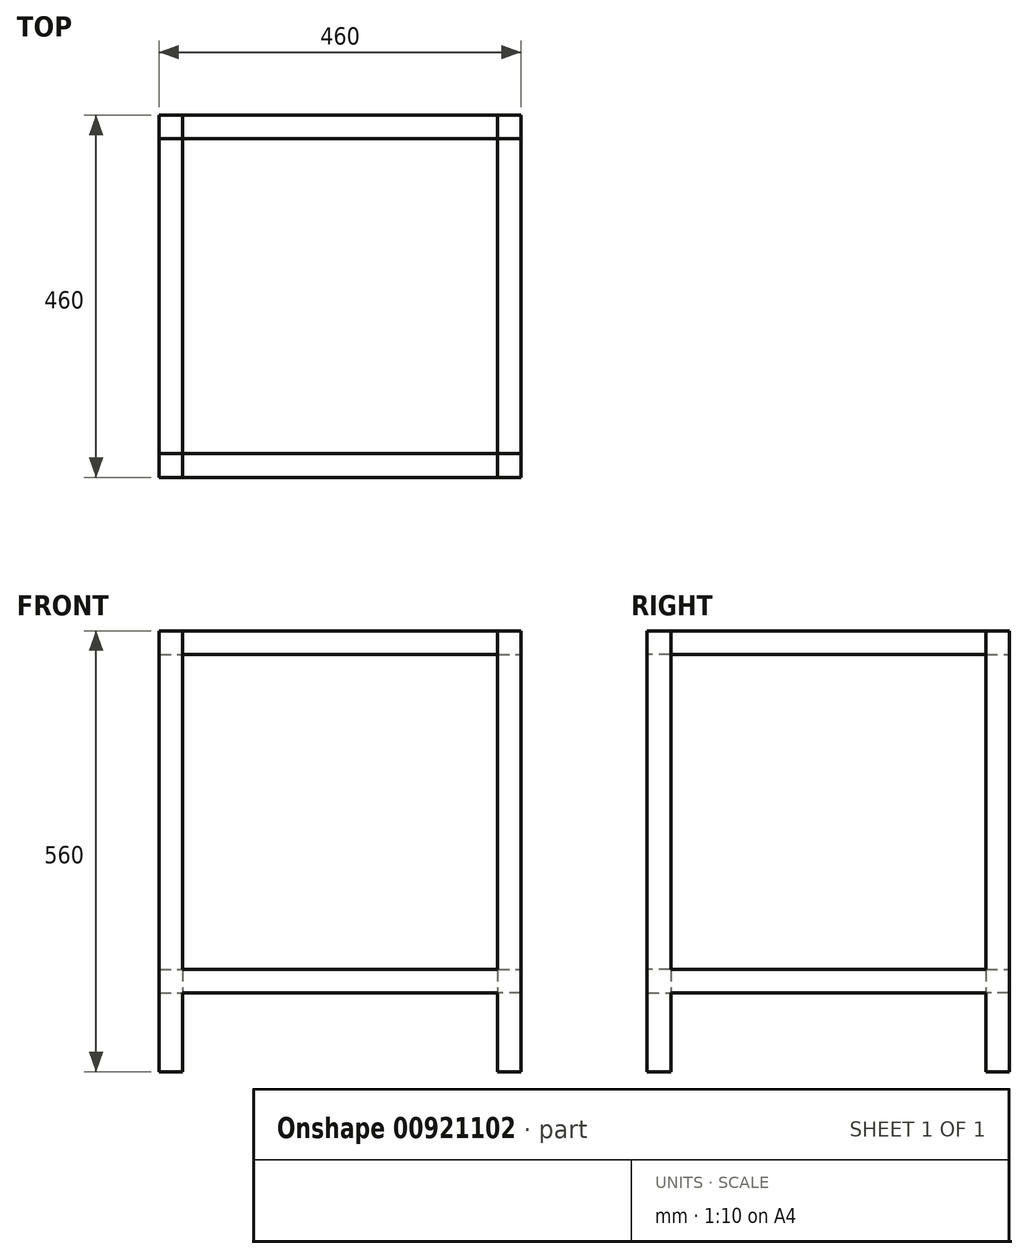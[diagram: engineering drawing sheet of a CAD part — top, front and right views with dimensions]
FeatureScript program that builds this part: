
annotation { "Feature Type Name" : "Feature", "Feature Type Description" : "" }
export const myFeature = defineFeature(function(context is Context, id is Id, definition is map)
    precondition{}
    {
        {
            assignVariable(context, id + "F0", {"variableType" : VariableType.LENGTH, "name" : "cubeInnerLength", "lengthValue" : 400 * mm});
        }
        {
            assignVariable(context, id + "F1", {"variableType" : VariableType.LENGTH, "name" : "aluminumProfileWidth", "lengthValue" : 30 * mm});
        }
        {
            assignVariable(context, id + "F2", {"variableType" : VariableType.LENGTH, "name" : "baseHeight", "lengthValue" : 100 * mm});
        }
        {
            var Q0;
            Q0=qCreatedBy(makeId("Top.planeOp"),FACE);
            var sketch = newSketch(context, id + "F3", { "sketchPlane" : qUnion([Q0])});
            skPoint(sketch, "E0.middle", {"position": v(0, 0) * mm});
            skLineSegment(sketch, "E1.bottom", {"start": v(-230, 230) * mm, "end": v(-200, 230) * mm});
            skLineSegment(sketch, "E1.top", {"start": v(-230, 200) * mm, "end": v(-200, 200) * mm});
            skLineSegment(sketch, "E1.left", {"start": v(-230, 230) * mm, "end": v(-230, 200) * mm});
            skLineSegment(sketch, "E1.right", {"start": v(-200, 230) * mm, "end": v(-200, 200) * mm});
            skLineSegment(sketch, "E2.bottom", {"start": v(230, 230) * mm, "end": v(200, 230) * mm});
            skLineSegment(sketch, "E2.top", {"start": v(230, 200) * mm, "end": v(200, 200) * mm});
            skLineSegment(sketch, "E2.left", {"start": v(230, 230) * mm, "end": v(230, 200) * mm});
            skLineSegment(sketch, "E2.right", {"start": v(200, 230) * mm, "end": v(200, 200) * mm});
            skLineSegment(sketch, "E3.bottom", {"start": v(230, -230) * mm, "end": v(200, -230) * mm});
            skLineSegment(sketch, "E3.top", {"start": v(230, -200) * mm, "end": v(200, -200) * mm});
            skLineSegment(sketch, "E3.left", {"start": v(230, -230) * mm, "end": v(230, -200) * mm});
            skLineSegment(sketch, "E3.right", {"start": v(200, -230) * mm, "end": v(200, -200) * mm});
            skLineSegment(sketch, "E4.bottom", {"start": v(-230, -230) * mm, "end": v(-200, -230) * mm});
            skLineSegment(sketch, "E4.top", {"start": v(-230, -200) * mm, "end": v(-200, -200) * mm});
            skLineSegment(sketch, "E4.left", {"start": v(-230, -230) * mm, "end": v(-230, -200) * mm});
            skLineSegment(sketch, "E4.right", {"start": v(-200, -230) * mm, "end": v(-200, -200) * mm});
            skLineSegment(sketch, "E5.bottom", {"start": v(-200, 200) * mm, "end": v(200, 200) * mm, "construction": true});
            skLineSegment(sketch, "E5.top", {"start": v(-200, -200) * mm, "end": v(200, -200) * mm, "construction": true});
            skLineSegment(sketch, "E5.left", {"start": v(-200, 200) * mm, "end": v(-200, -200) * mm, "construction": true});
            skLineSegment(sketch, "E5.right", {"start": v(200, 200) * mm, "end": v(200, -200) * mm, "construction": true});
            skSolve(sketch);
        }
        {
            var Q0;
            {var subQ4=sQuery(id+"F3.wireOp",EDGE,"E1.top");Q0=makeQuery(id+"F3.imprint","IMPRINT",FACE,{"disambiguationData":[TD([[makeQuery(id+"F3.imprint","IMPRINT",EDGE,{"derivedFrom":subQ4}),1.0]])]});}
            var Q1;
            {var subQ4=sQuery(id+"F3.wireOp",EDGE,"E2.top");Q1=makeQuery(id+"F3.imprint","IMPRINT",FACE,{"disambiguationData":[TD([[makeQuery(id+"F3.imprint","IMPRINT",EDGE,{"derivedFrom":subQ4}),-1.0]])]});}
            var Q2;
            {var subQ4=sQuery(id+"F3.wireOp",EDGE,"E3.top");Q2=makeQuery(id+"F3.imprint","IMPRINT",FACE,{"disambiguationData":[TD([[makeQuery(id+"F3.imprint","IMPRINT",EDGE,{"derivedFrom":subQ4}),1.0]])]});}
            var Q3;
            {var subQ4=sQuery(id+"F3.wireOp",EDGE,"E4.top");Q3=makeQuery(id+"F3.imprint","IMPRINT",FACE,{"disambiguationData":[TD([[makeQuery(id+"F3.imprint","IMPRINT",EDGE,{"derivedFrom":subQ4}),-1.0]])]});}
            extrude(context, id + "F4", {"entities" : qUnion([Q0, Q1, Q2, Q3]), "depth" : getVariable(context, 'cubeInnerLength') + 2 * getVariable(context, 'aluminumProfileWidth'), "offsetDistance" : 25 * mm, "symmetric" : true});
        }
        {
            var Q0;
            Q0=qCreatedBy(makeId("Front.planeOp"),FACE);
            var sketch = newSketch(context, id + "F5", { "sketchPlane" : qUnion([Q0])});
            skLineSegment(sketch, "E6.bottom", {"start": v(-230, 230) * mm, "end": v(-200, 230) * mm});
            skLineSegment(sketch, "E6.top", {"start": v(-230, 200) * mm, "end": v(-200, 200) * mm});
            skLineSegment(sketch, "E6.left", {"start": v(-230, 230) * mm, "end": v(-230, 200) * mm});
            skLineSegment(sketch, "E6.right", {"start": v(-200, 230) * mm, "end": v(-200, 200) * mm});
            skLineSegment(sketch, "E7.bottom", {"start": v(200, 230) * mm, "end": v(230, 230) * mm});
            skLineSegment(sketch, "E7.top", {"start": v(200, 200) * mm, "end": v(230, 200) * mm});
            skLineSegment(sketch, "E7.left", {"start": v(200, 230) * mm, "end": v(200, 200) * mm});
            skLineSegment(sketch, "E7.right", {"start": v(230, 230) * mm, "end": v(230, 200) * mm});
            skLineSegment(sketch, "E8.bottom", {"start": v(-230, -200) * mm, "end": v(-200, -200) * mm});
            skLineSegment(sketch, "E8.top", {"start": v(-230, -230) * mm, "end": v(-200, -230) * mm});
            skLineSegment(sketch, "E8.left", {"start": v(-230, -200) * mm, "end": v(-230, -230) * mm});
            skLineSegment(sketch, "E8.right", {"start": v(-200, -200) * mm, "end": v(-200, -230) * mm});
            skLineSegment(sketch, "E9.bottom", {"start": v(200, -200) * mm, "end": v(230, -200) * mm});
            skLineSegment(sketch, "E9.top", {"start": v(200, -230) * mm, "end": v(230, -230) * mm});
            skLineSegment(sketch, "E9.left", {"start": v(200, -200) * mm, "end": v(200, -230) * mm});
            skLineSegment(sketch, "E9.right", {"start": v(230, -200) * mm, "end": v(230, -230) * mm});
            skLineSegment(sketch, "E10.bottom", {"start": v(-200, 200) * mm, "end": v(200, 200) * mm, "construction": true});
            skLineSegment(sketch, "E10.top", {"start": v(-200, -200) * mm, "end": v(200, -200) * mm, "construction": true});
            skLineSegment(sketch, "E10.left", {"start": v(-200, 200) * mm, "end": v(-200, -200) * mm, "construction": true});
            skLineSegment(sketch, "E10.right", {"start": v(200, 200) * mm, "end": v(200, -200) * mm, "construction": true});
            skPoint(sketch, "E10.middle", {"position": v(0, 0) * mm});
            skSolve(sketch);
        }
        {
            var Q0;
            Q0 = qSketchRegion(id + "F5", true);
            extrude(context, id + "F6", {"entities" : qUnion([Q0]), "depth" : getVariable(context, 'cubeInnerLength'), "offsetDistance" : 25 * mm, "symmetric" : true});
        }
        {
            var Q0;
            Q0=qCreatedBy(makeId("Right.planeOp"),FACE);
            var sketch = newSketch(context, id + "F7", { "sketchPlane" : qUnion([Q0])});
            skLineSegment(sketch, "E11.bottom", {"start": v(200, 200) * mm, "end": v(-200, 200) * mm, "construction": true});
            skLineSegment(sketch, "E11.top", {"start": v(200, -200) * mm, "end": v(-200, -200) * mm, "construction": true});
            skLineSegment(sketch, "E11.left", {"start": v(200, 200) * mm, "end": v(200, -200) * mm, "construction": true});
            skLineSegment(sketch, "E11.right", {"start": v(-200, 200) * mm, "end": v(-200, -200) * mm, "construction": true});
            skPoint(sketch, "E11.middle", {"position": v(0, 0) * mm});
            skLineSegment(sketch, "E12.bottom", {"start": v(-200, 200) * mm, "end": v(-230, 200) * mm});
            skLineSegment(sketch, "E12.top", {"start": v(-200, 230) * mm, "end": v(-230, 230) * mm});
            skLineSegment(sketch, "E12.left", {"start": v(-200, 200) * mm, "end": v(-200, 230) * mm});
            skLineSegment(sketch, "E12.right", {"start": v(-230, 200) * mm, "end": v(-230, 230) * mm});
            skLineSegment(sketch, "E13.bottom", {"start": v(200, 200) * mm, "end": v(230, 200) * mm});
            skLineSegment(sketch, "E13.top", {"start": v(200, 230) * mm, "end": v(230, 230) * mm});
            skLineSegment(sketch, "E13.left", {"start": v(200, 200) * mm, "end": v(200, 230) * mm});
            skLineSegment(sketch, "E13.right", {"start": v(230, 200) * mm, "end": v(230, 230) * mm});
            skLineSegment(sketch, "E14.bottom", {"start": v(200, -200) * mm, "end": v(230, -200) * mm});
            skLineSegment(sketch, "E14.top", {"start": v(200, -230) * mm, "end": v(230, -230) * mm});
            skLineSegment(sketch, "E14.left", {"start": v(200, -200) * mm, "end": v(200, -230) * mm});
            skLineSegment(sketch, "E14.right", {"start": v(230, -200) * mm, "end": v(230, -230) * mm});
            skLineSegment(sketch, "E15.bottom", {"start": v(-200, -200) * mm, "end": v(-230, -200) * mm});
            skLineSegment(sketch, "E15.top", {"start": v(-200, -230) * mm, "end": v(-230, -230) * mm});
            skLineSegment(sketch, "E15.left", {"start": v(-200, -200) * mm, "end": v(-200, -230) * mm});
            skLineSegment(sketch, "E15.right", {"start": v(-230, -200) * mm, "end": v(-230, -230) * mm});
            skSolve(sketch);
        }
        {
            var Q0;
            Q0 = qSketchRegion(id + "F7", true);
            extrude(context, id + "F8", {"entities" : qUnion([Q0]), "depth" : getVariable(context, 'cubeInnerLength'), "offsetDistance" : 25 * mm, "symmetric" : true});
        }
        {
            var Q0;
            Q0=makeQuery(id+"F4.opExtrude","CAP_FACE",FACE,{"disambiguationData":[OSD([sQuery(id+"F3.wireOp",EDGE,"E4.bottom"),sQuery(id+"F3.wireOp",EDGE,"E4.top"),sQuery(id+"F3.wireOp",EDGE,"E4.left"),sQuery(id+"F3.wireOp",EDGE,"E4.right")])],"isStart":true});
            var Q1;
            Q1=makeQuery(id+"F4.opExtrude","CAP_FACE",FACE,{"disambiguationData":[OSD([sQuery(id+"F3.wireOp",EDGE,"E3.bottom"),sQuery(id+"F3.wireOp",EDGE,"E3.top"),sQuery(id+"F3.wireOp",EDGE,"E3.left"),sQuery(id+"F3.wireOp",EDGE,"E3.right")])],"isStart":true});
            var Q2;
            Q2=makeQuery(id+"F4.opExtrude","CAP_FACE",FACE,{"disambiguationData":[OSD([sQuery(id+"F3.wireOp",EDGE,"E1.bottom"),sQuery(id+"F3.wireOp",EDGE,"E1.top"),sQuery(id+"F3.wireOp",EDGE,"E1.left"),sQuery(id+"F3.wireOp",EDGE,"E1.right")])],"isStart":true});
            var Q3;
            Q3=makeQuery(id+"F4.opExtrude","CAP_FACE",FACE,{"disambiguationData":[OSD([sQuery(id+"F3.wireOp",EDGE,"E2.bottom"),sQuery(id+"F3.wireOp",EDGE,"E2.top"),sQuery(id+"F3.wireOp",EDGE,"E2.left"),sQuery(id+"F3.wireOp",EDGE,"E2.right")])],"isStart":true});
            extrude(context, id + "F9", {"entities" : qUnion([Q0, Q1, Q2, Q3]), "operationType" : NewBodyOperationType.ADD, "depth" : getVariable(context, 'baseHeight'), "offsetDistance" : 25 * mm});
        }
    });
